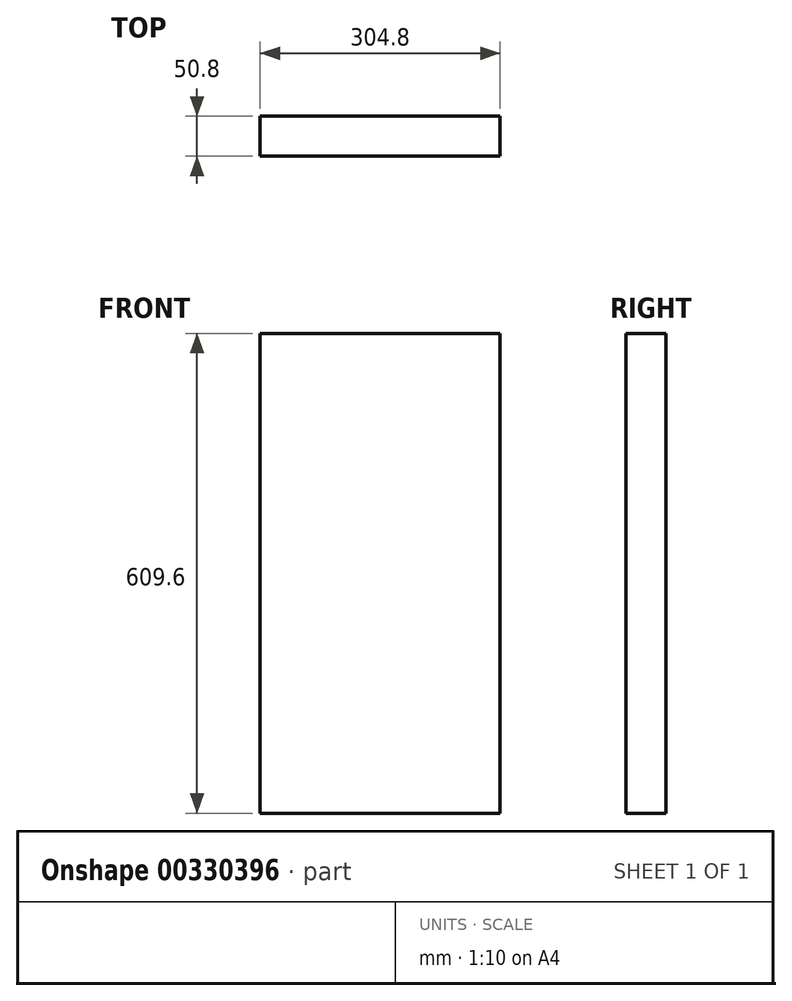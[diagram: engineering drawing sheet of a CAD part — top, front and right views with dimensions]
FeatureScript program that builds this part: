
annotation { "Feature Type Name" : "Feature", "Feature Type Description" : "" }
export const myFeature = defineFeature(function(context is Context, id is Id, definition is map)
    precondition{}
    {
        {
            var Q0;
            Q0=qCreatedBy(makeId("Front.planeOp"),FACE);
            var sketch = newSketch(context, id + "F0", { "sketchPlane" : qUnion([Q0])});
            skLineSegment(sketch, "E0.bottom", {"start": v(-149.66, 375.02) * mm, "end": v(155.14, 375.02) * mm});
            skLineSegment(sketch, "E0.top", {"start": v(-149.66, -234.58) * mm, "end": v(155.14, -234.58) * mm});
            skLineSegment(sketch, "E0.left", {"start": v(-149.66, 375.02) * mm, "end": v(-149.66, -234.58) * mm});
            skLineSegment(sketch, "E0.right", {"start": v(155.14, 375.02) * mm, "end": v(155.14, -234.58) * mm});
            skSolve(sketch);
        }
        {
            var Q0;
            Q0=makeQuery(id+"F0.imprint","IMPRINT",FACE,{"disambiguationData":[TD([[makeQuery(id+"F0.imprint","IMPRINT",EDGE,{"derivedFrom":sQuery(id+"F0.wireOp",EDGE,"E0.bottom")}),-1.0]])]});
            extrude(context, id + "F1", {"entities" : qUnion([Q0]), "depth" : 50.8 * mm});
        }
    });
